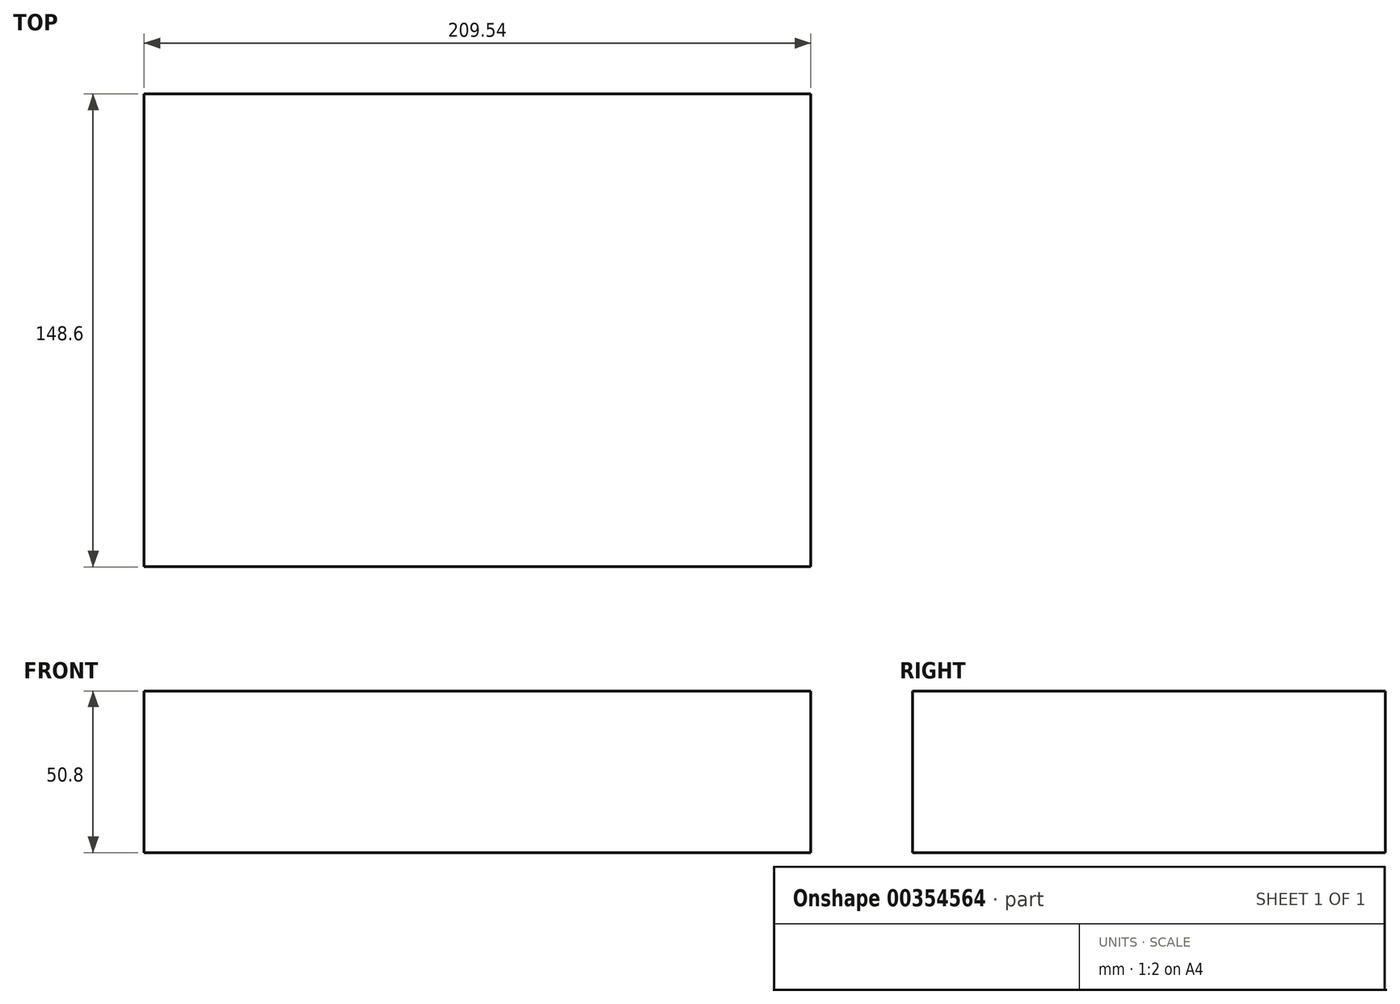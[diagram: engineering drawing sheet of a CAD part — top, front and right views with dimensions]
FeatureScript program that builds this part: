
annotation { "Feature Type Name" : "Feature", "Feature Type Description" : "" }
export const myFeature = defineFeature(function(context is Context, id is Id, definition is map)
    precondition{}
    {
        {
            var Q0;
            Q0=qCreatedBy(makeId("Top.planeOp"),FACE);
            var sketch = newSketch(context, id + "F0", { "sketchPlane" : qUnion([Q0])});
            skLineSegment(sketch, "E0.bottom", {"start": v(104.78, 74.3) * mm, "end": v(-104.77, 74.3) * mm});
            skLineSegment(sketch, "E0.top", {"start": v(104.77, -74.3) * mm, "end": v(-104.78, -74.3) * mm});
            skLineSegment(sketch, "E0.left", {"start": v(104.78, 74.3) * mm, "end": v(104.77, -74.3) * mm});
            skLineSegment(sketch, "E0.right", {"start": v(-104.77, 74.3) * mm, "end": v(-104.78, -74.3) * mm});
            skPoint(sketch, "E0.middle", {"position": v(0, 0) * mm});
            skSolve(sketch);
        }
        {
            var Q0;
            Q0=makeQuery(id+"F0.imprint","IMPRINT",FACE,{"disambiguationData":[TD([[makeQuery(id+"F0.imprint","IMPRINT",EDGE,{"derivedFrom":sQuery(id+"F0.wireOp",EDGE,"E0.bottom")}),1.0]])]});
            extrude(context, id + "F1", {"entities" : qUnion([Q0]), "depth" : 50.8 * mm});
        }
    });
